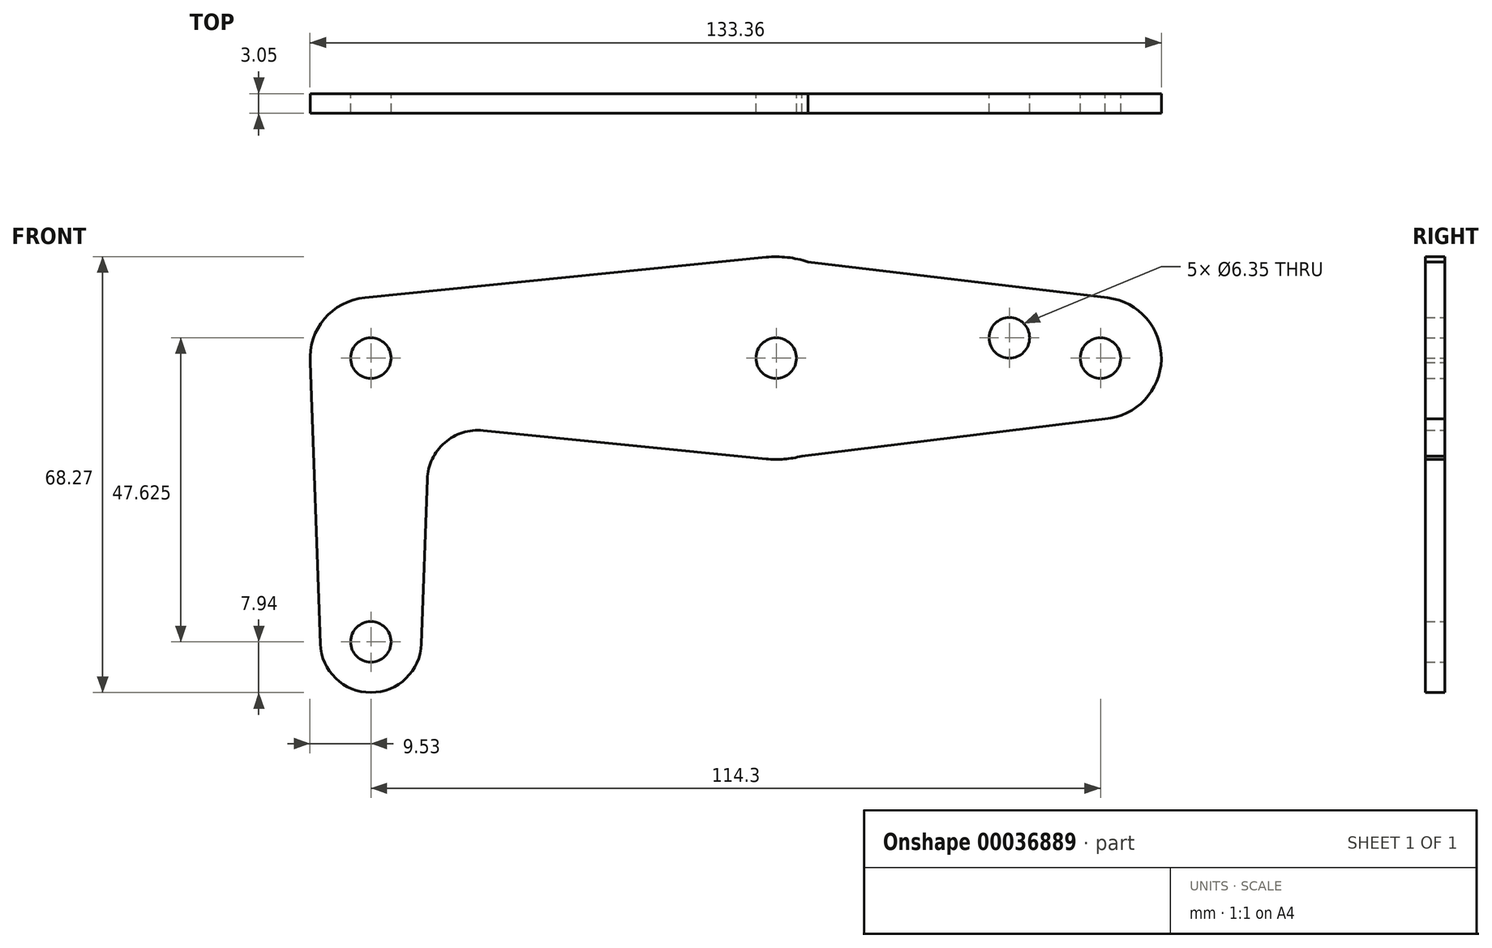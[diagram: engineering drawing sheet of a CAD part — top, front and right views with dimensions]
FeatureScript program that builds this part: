
annotation { "Feature Type Name" : "Feature", "Feature Type Description" : "" }
export const myFeature = defineFeature(function(context is Context, id is Id, definition is map)
    precondition{}
    {
        {
            var Q0;
            Q0=qCreatedBy(makeId("Front.planeOp"),FACE);
            var sketch = newSketch(context, id + "F0", { "sketchPlane" : qUnion([Q0])});
            skLineSegment(sketch, "E0", {"start": v(0, 0) * mm, "end": v(114.3, 0) * mm, "construction": true});
            skLineSegment(sketch, "E1", {"start": v(0, 0) * mm, "end": v(0, -44.45) * mm, "construction": true});
            skCircle(sketch, "E2", {"center": v(114.3, 0) * mm, "radius": 9.53 * mm});
            skCircle(sketch, "E3", {"center": v(0, 0) * mm, "radius": 9.53 * mm});
            skCircle(sketch, "E4", {"center": v(0, -44.45) * mm, "radius": 7.94 * mm});
            skCircle(sketch, "E5", {"center": v(63.5, 0) * mm, "radius": 15.88 * mm});
            skLineSegment(sketch, "E6", {"start": v(8.85, -18.97) * mm, "end": v(7.93, -44.73) * mm});
            skLineSegment(sketch, "E7", {"start": v(-9.53, 0) * mm, "end": v(-7.93, -44.73) * mm});
            skCircle(sketch, "E8", {"center": v(114.3, 0) * mm, "radius": 3.18 * mm});
            skCircle(sketch, "E9", {"center": v(63.5, 0) * mm, "radius": 3.18 * mm});
            skCircle(sketch, "E10", {"center": v(0, 0) * mm, "radius": 3.18 * mm});
            skCircle(sketch, "E11", {"center": v(0, -44.45) * mm, "radius": 3.18 * mm});
            skCircle(sketch, "E12", {"center": v(100.03, 3.18) * mm, "radius": 3.18 * mm});
            skLineSegment(sketch, "E13", {"start": v(115.43, 9.46) * mm, "end": v(62.2, 15.82) * mm});
            skLineSegment(sketch, "E14", {"start": v(115.03, -9.5) * mm, "end": v(63.32, -15.87) * mm});
            skLineSegment(sketch, "E15", {"start": v(61.91, 15.8) * mm, "end": v(-0.95, 9.48) * mm});
            skLineSegment(sketch, "E16", {"start": v(61.91, -15.8) * mm, "end": v(17.59, -11.34) * mm});
            skArc(sketch, "E17.filletArc", {"start": v(17.59, -11.34) * mm, "mid": v(11.57, -13.26) * mm, "end": v(8.85, -18.97) * mm});
            skSolve(sketch);
        }
        {
            var Q0;
            Q0 = qSketchRegion(id + "F0", true);
            extrude(context, id + "F1", {"entities" : qUnion([Q0]), "depth" : 3.05 * mm});
        }
    });
